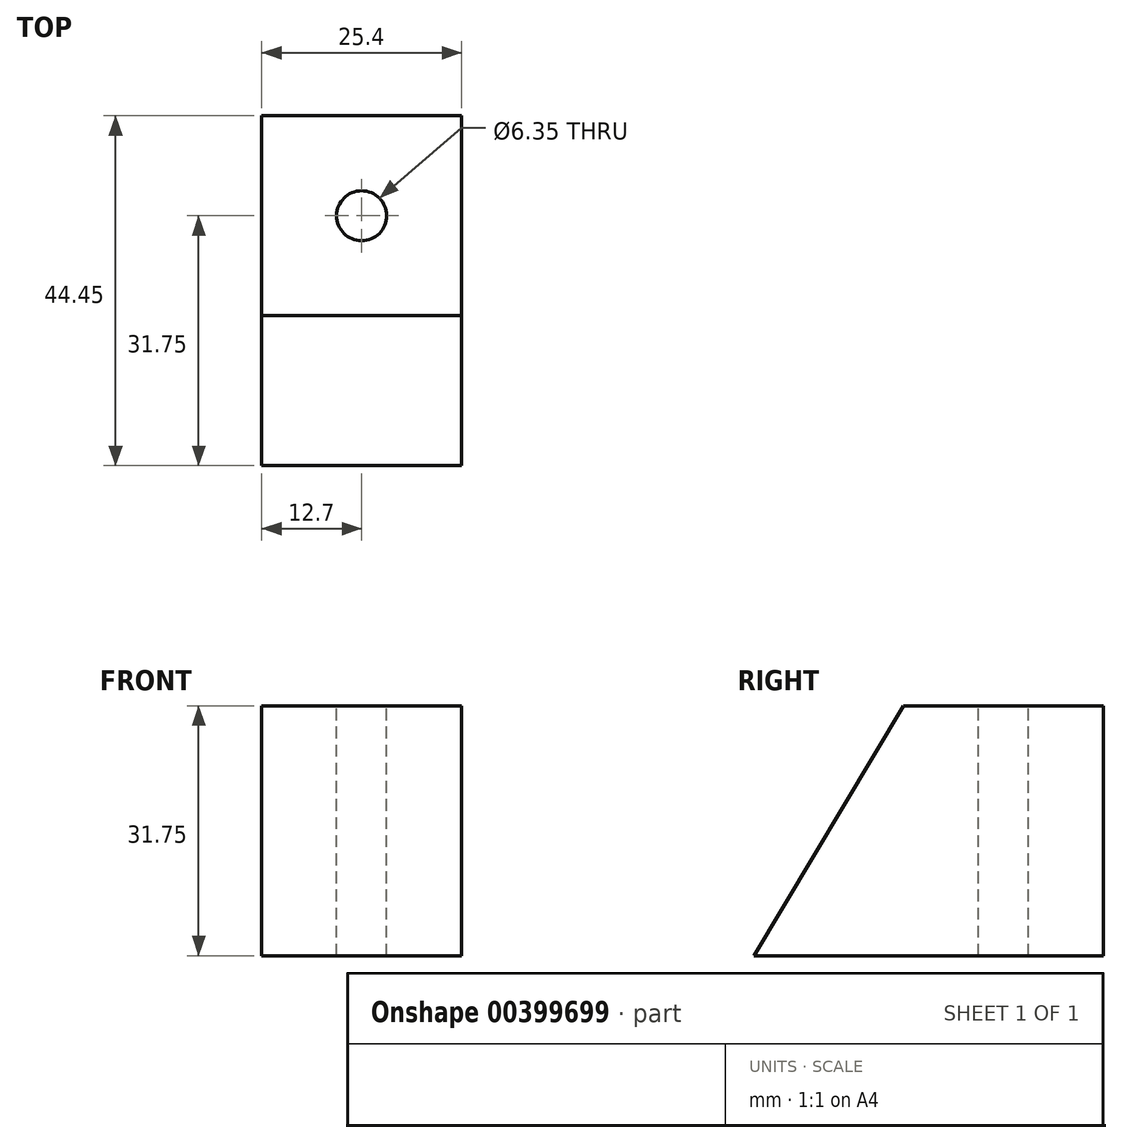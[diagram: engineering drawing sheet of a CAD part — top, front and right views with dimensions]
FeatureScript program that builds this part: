
annotation { "Feature Type Name" : "Feature", "Feature Type Description" : "" }
export const myFeature = defineFeature(function(context is Context, id is Id, definition is map)
    precondition{}
    {
        {
            var Q0;
            Q0=qCreatedBy(makeId("Right.planeOp"),FACE);
            var sketch = newSketch(context, id + "F0", { "sketchPlane" : qUnion([Q0])});
            skLineSegment(sketch, "E0", {"start": v(0, 0) * mm, "end": v(0, 31.75) * mm});
            skLineSegment(sketch, "E1", {"start": v(0, 31.75) * mm, "end": v(-25.4, 31.75) * mm});
            skLineSegment(sketch, "E2", {"start": v(-25.4, 31.75) * mm, "end": v(-44.45, 0) * mm});
            skLineSegment(sketch, "E3", {"start": v(-44.45, 0) * mm, "end": v(0, 0) * mm});
            skSolve(sketch);
        }
        {
            var Q0;
            Q0=makeQuery(id+"F0.imprint","IMPRINT",FACE,{"disambiguationData":[TD([[makeQuery(id+"F0.imprint","IMPRINT",EDGE,{"derivedFrom":sQuery(id+"F0.wireOp",EDGE,"E0")}),1.0]])]});
            extrude(context, id + "F1", {"entities" : qUnion([Q0]), "depth" : 25.4 * mm});
        }
        {
            var Q0;
            Q0=makeQuery(id+"F1.opExtrude","SWEPT_FACE",FACE,{"disambiguationData":[OSD([sQuery(id+"F0.wireOp",EDGE,"E1")])]});
            var sketch = newSketch(context, id + "F2", { "sketchPlane" : qUnion([Q0])});
            skLineSegment(sketch, "E4", {"start": v(12.7, 0) * mm, "end": v(12.7, -25.4) * mm, "construction": true});
            skLineSegment(sketch, "E5", {"start": v(0, -12.7) * mm, "end": v(25.4, -12.7) * mm, "construction": true});
            skCircle(sketch, "E6", {"center": v(12.7, -12.7) * mm, "radius": 3.18 * mm});
            skSolve(sketch);
        }
        {
            var Q0;
            Q0=sQuery(id+"F2.wireOp",VERTEX,"E6.center");
            var Q1;
            Q1=makeQuery(id+"F1.opExtrude","SWEPT_BODY",BODY,{"disambiguationData":[OSD([sQuery(id+"F0.wireOp",EDGE,"E0"),sQuery(id+"F0.wireOp",EDGE,"E1"),sQuery(id+"F0.wireOp",EDGE,"E2"),sQuery(id+"F0.wireOp",EDGE,"E3")])]});
            hole(context, id + "F3", {"style" : HoleStyle.SIMPLE, "endStyle" : HoleEndStyle.THROUGH, "holeDiameter" : 6.35 * mm, "isTappedThrough" : true, "tappedDepth" : 12.7 * mm, "tapClearance" : 3, "locations" : qUnion([Q0]), "scope" : qUnion([Q1])});
        }
    });
